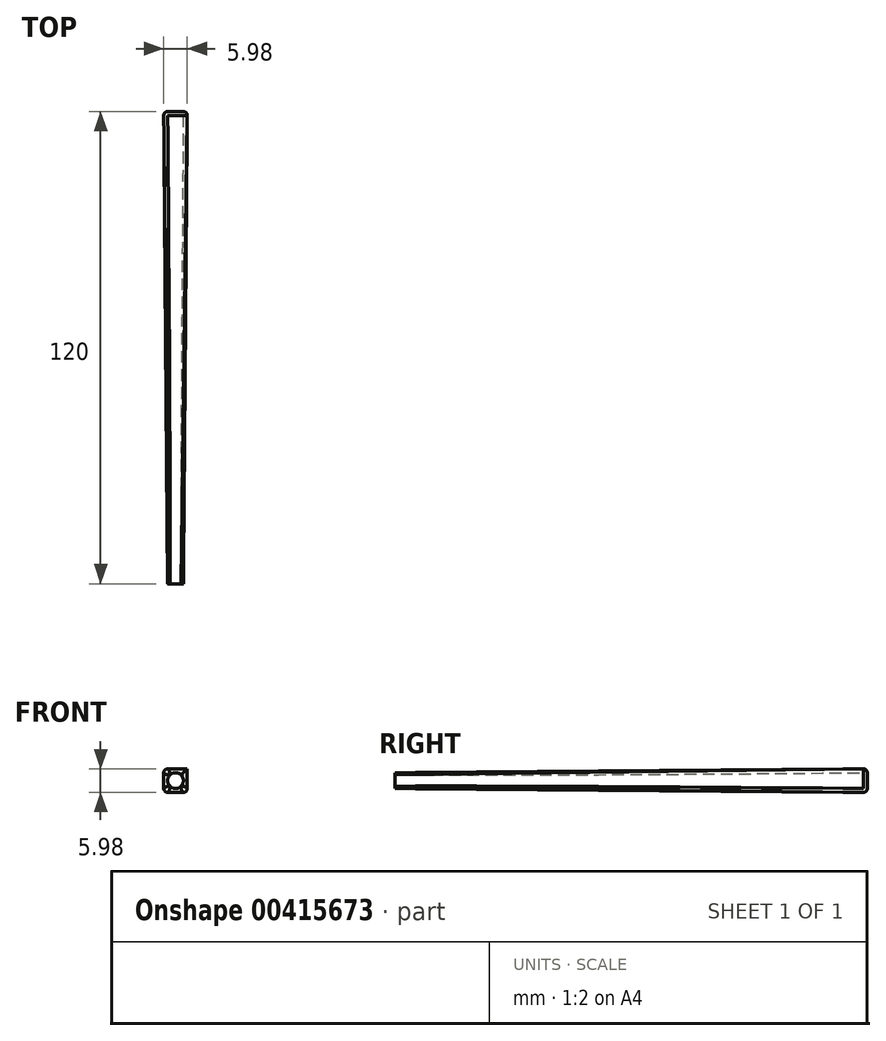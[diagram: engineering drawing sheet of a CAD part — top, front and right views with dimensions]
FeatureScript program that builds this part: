
annotation { "Feature Type Name" : "Feature", "Feature Type Description" : "" }
export const myFeature = defineFeature(function(context is Context, id is Id, definition is map)
    precondition{}
    {
        {
            var Q0;
            Q0=qCreatedBy(makeId("Front.planeOp"),FACE);
            cPlane(context, id + "F0", {"entities" : qUnion([Q0]), "cplaneType" : CPlaneType.OFFSET, "offset" : 120 * mm, "width" : 150 * mm, "height" : 150 * mm});
        }
        {
            var Q0;
            Q0=qCreatedBy(makeId("Front.planeOp"),FACE);
            var sketch = newSketch(context, id + "F1", { "sketchPlane" : qUnion([Q0])});
            skLineSegment(sketch, "E0.bottom", {"start": v(-3, 3) * mm, "end": v(3, 3) * mm});
            skLineSegment(sketch, "E0.top", {"start": v(-3, -3) * mm, "end": v(3, -3) * mm});
            skLineSegment(sketch, "E0.left", {"start": v(-3, 3) * mm, "end": v(-3, -3) * mm});
            skLineSegment(sketch, "E0.right", {"start": v(3, 3) * mm, "end": v(3, -3) * mm});
            skPoint(sketch, "E0.middle", {"position": v(0, 0) * mm});
            skSolve(sketch);
        }
        {
            var Q0;
            Q0=qCreatedBy(id+"F0.planeOp",FACE);
            var sketch = newSketch(context, id + "F2", { "sketchPlane" : qUnion([Q0])});
            skCircle(sketch, "E1", {"center": v(0, 0) * mm, "radius": 2 * mm});
            skSolve(sketch);
        }
        {
            var Q0;
            Q0=makeQuery(id+"F2.imprint","IMPRINT",FACE,{"disambiguationData":[TD([[makeQuery(id+"F2.imprint","IMPRINT",EDGE,{"derivedFrom":sQuery(id+"F2.wireOp",EDGE,"E1")}),1.0]])]});
            var Q1;
            Q1=makeQuery(id+"F1.imprint","IMPRINT",FACE,{"disambiguationData":[TD([[makeQuery(id+"F1.imprint","IMPRINT",EDGE,{"derivedFrom":sQuery(id+"F1.wireOp",EDGE,"E0.bottom")}),-1.0]])]});
            loft(context, id + "F3", {"sheetProfilesArray" : [{ "sheetProfileEntities" : qUnion([Q0]) }, { "sheetProfileEntities" : qUnion([Q1]) }]});
        }
        {
            var Q0;
            Q0=makeQuery(id+"F3.opLoft","SWEPT_EDGE",EDGE,{"disambiguationData":[OSD([sQuery(id+"F1.wireOp",EDGE,"E0.bottom"),sQuery(id+"F1.wireOp",EDGE,"E0.left"),sQuery(id+"F1.wireOp",EDGE,"E0.right"),sQuery(id+"F2.wireOp",EDGE,"E1")])]});
            var Q1;
            Q1=makeQuery(id+"F3.opLoft","SWEPT_EDGE",EDGE,{"disambiguationData":[OSD([sQuery(id+"F1.wireOp",EDGE,"E0.bottom"),sQuery(id+"F1.wireOp",EDGE,"E0.left")])]});
            var Q2;
            Q2=makeQuery(id+"F3.opLoft","SWEPT_EDGE",EDGE,{"disambiguationData":[OSD([sQuery(id+"F1.wireOp",EDGE,"E0.bottom"),sQuery(id+"F1.wireOp",EDGE,"E0.top"),sQuery(id+"F1.wireOp",EDGE,"E0.right"),sQuery(id+"F2.wireOp",EDGE,"E1")])]});
            var Q3;
            Q3=makeQuery(id+"F3.opLoft","SWEPT_EDGE",EDGE,{"disambiguationData":[OSD([sQuery(id+"F1.wireOp",EDGE,"E0.top"),sQuery(id+"F1.wireOp",EDGE,"E0.left"),sQuery(id+"F1.wireOp",EDGE,"E0.right"),sQuery(id+"F2.wireOp",EDGE,"E1")])]});
            var Q4;
            Q4=makeQuery(id+"F3.opLoft","CAP_FACE",FACE,{"disambiguationData":[OSD([makeQuery(id+"F1.imprint","IMPRINT",FACE,{"disambiguationData":[TD([[makeQuery(id+"F1.imprint","IMPRINT",EDGE,{"derivedFrom":sQuery(id+"F1.wireOp",EDGE,"E0.bottom")}),-1.0]])]})])],"isStart":true});
            fillet(context, id + "F4", {"entities" : qUnion([Q0, Q1, Q2, Q3, Q4]), "radius" : 1 * mm, "tangentPropagation" : true, "allowEdgeOverflow" : false});
        }
    });
